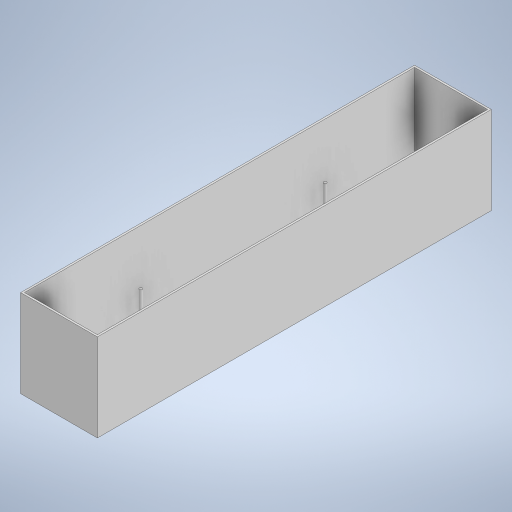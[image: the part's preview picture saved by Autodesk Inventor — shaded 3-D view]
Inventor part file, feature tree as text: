
AUTODESK INVENTOR PART (.ipt)
format: ipt  version: 2023 (Build 270158030, 158C)  size: 267,264 bytes
history: native  units: in
note: dims shown in document units (in); Inventor stores cm internally (conversion verified against a paired STEP export)
features: extrude x5, sketch x2
ambient origin geometry x8: Origin, YZ Plane, XZ Plane, XY Plane, X Axis, Y Axis, Z Axis, Center Point
bodies: Solid1 (feature_tree)
feature tree (7):
  extrude  "Extrusion1"  Depth=25.65in
  extrude  "Extrusion2"  Depth=0.125in TaperAngle=0.0deg
  extrude  "Extrusion3"  Depth=5.7in TaperAngle=0.0deg
  extrude  "Extrusion4"  Depth=1.0in
  extrude  "Extrusion5"  Depth=0.5in
  sketch  "Sketch2"  dims[d0=5.0in d1=25.65in]
  sketch  "Sketch3"  dims[d2=0.125in d3=0.125in d4=0.0in d5=5.7in d6=0.0in d7=1.0in d8=0.5in d9=2.0in d10=3.0in d11=0.5in d12=0.0in d13=0.1875in d14=0.1875in d15=3.0in d16=1.0in d17=6.0in d18=3.0in d19=0.0in d20=2.0in d21=2.5in d22=0.75in d23=0.0in]
